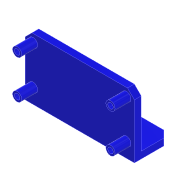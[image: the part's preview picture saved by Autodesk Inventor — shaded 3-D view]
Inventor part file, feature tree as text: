
AUTODESK INVENTOR PART (.ipt)
format: ipt  version: 2022 (Build 260153000, 153)  size: 204,800 bytes
history: native  units: mm
features: sketch x5, extrude x3, hole x2, chamfer x2, projected_geometry x2, rib x1
ambient origin geometry x8: Origin, YZ Plane, XZ Plane, XY Plane, X Axis, Y Axis, Z Axis, Center Point
bodies: Solid1 (feature_tree)
feature tree (15):
  extrude  "Extrusion1"  Depth=44.0mm
  extrude  "Extrusion2"  Depth=3.0mm TaperAngle=0.0deg
  hole  "Hole1"  [1 undecoded]
  rib  "Rib1"
  chamfer  "Chamfer1"  Distance=2.0mm
  hole  "Hole2"  [1 undecoded]
  chamfer  "Chamfer2"  Distance=10.0mm
  extrude  "Extrusion3"  Depth=7.0mm
  sketch  "Sketch1"  dims[d0=20.0mm d1=44.0mm]
  sketch  "Sketch2"  dims[d2=2.0mm d3=3.0mm d4=0.0mm]
  sketch  "Sketch3"  dims[d5=16.0mm d6=3.0mm d7=0.0mm]
  sketch  "Sketch5"  dims[d8=2.0mm]
  sketch  "Sketch6"  dims[d9=2.0mm d10=2.0mm d11=2.0mm d14=2.4mm d15=6.0mm d16=4.0mm d17=2.0mm d18=90.0deg d19=6.0mm d20=0.0mm d21=10.0mm d22=15.0mm d23=1.0mm d24=5.0mm d25=0.0mm d26=0.0mm d27=1.0mm d28=1.0mm d29=2.0mm d30=2.0mm d31=45.0deg d32=30.0mm d33=3.4mm d34=6.0mm d35=4.0mm d36=2.0mm d37=90.0deg d38=6.0mm d39=0.0mm d40=3.0mm d41=2.0mm d42=45.0deg d43=0.5mm d44=44.0mm d45=20.0mm d46=4.0mm d47=4.0mm d49=4.0mm d50=4.0mm d51=7.0mm d52=0.0mm]
  projected_geometry  "Project Cut Edges1"
  projected_geometry  "Project Cut Edges2"
note: 2 required parameter values undecoded (feature->parameter linkage not recoverable at this tier; creation-order binding heuristic only, values carry confidence <= 0.55)
